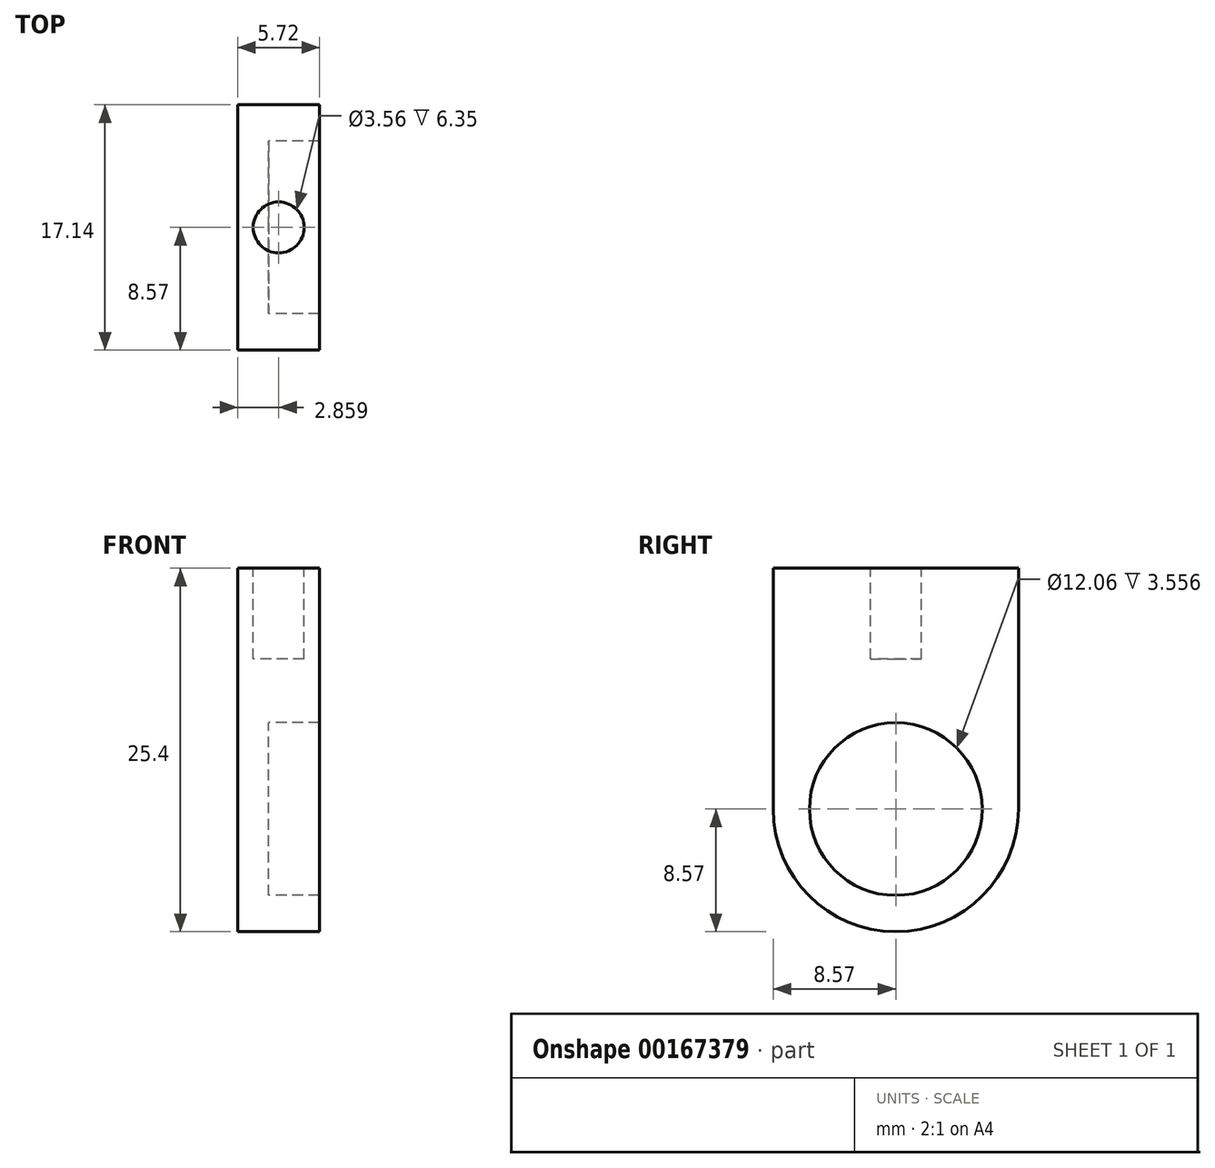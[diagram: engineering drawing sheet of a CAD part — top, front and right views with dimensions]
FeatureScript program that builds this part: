
annotation { "Feature Type Name" : "Feature", "Feature Type Description" : "" }
export const myFeature = defineFeature(function(context is Context, id is Id, definition is map)
    precondition{}
    {
        {
            var Q0;
            Q0=qCreatedBy(makeId("Right.planeOp"),FACE);
            var sketch = newSketch(context, id + "F0", { "sketchPlane" : qUnion([Q0])});
            skCircle(sketch, "E0", {"center": v(0, 0) * mm, "radius": 6.03 * mm});
            skCircle(sketch, "E1", {"center": v(0, 0) * mm, "radius": 8.57 * mm});
            skLineSegment(sketch, "E2.top", {"start": v(-8.57, 16.83) * mm, "end": v(8.57, 16.83) * mm});
            skLineSegment(sketch, "E2.left", {"start": v(-8.57, 0) * mm, "end": v(-8.57, 16.83) * mm});
            skLineSegment(sketch, "E2.right", {"start": v(8.57, 0) * mm, "end": v(8.57, 16.83) * mm});
            skSolve(sketch);
        }
        {
            var Q0;
            Q0 = qSketchRegion(id + "F0", true);
            extrude(context, id + "F1", {"entities" : qUnion([Q0]), "depth" : 3.56 * mm});
        }
        {
            var Q0;
            Q0=makeQuery(id+"F1.opExtrude","CAP_FACE",FACE,{"disambiguationData":[OSD([sQuery(id+"F0.wireOp",EDGE,"E0"),sQuery(id+"F0.wireOp",EDGE,"PU44gY0B-mLXA-vG6P-Z8EY-Ho4tR6I2Q1Xl.bottom"),sQuery(id+"F0.wireOp",EDGE,"PU44gY0B-mLXA-vG6P-Z8EY-Ho4tR6I2Q1Xl.top"),sQuery(id+"F0.wireOp",EDGE,"PU44gY0B-mLXA-vG6P-Z8EY-Ho4tR6I2Q1Xl.left"),sQuery(id+"F0.wireOp",EDGE,"PU44gY0B-mLXA-vG6P-Z8EY-Ho4tR6I2Q1Xl.right")])],"isStart":true});
            var Q1;
            Q1=makeQuery(id+"F0.imprint","IMPRINT",FACE,{"disambiguationData":[TD([[makeQuery(id+"F0.imprint","IMPRINT",EDGE,{"derivedFrom":sQuery(id+"F0.wireOp",EDGE,"E0")}),1.0]])]});
            extrude(context, id + "F2", {"entities" : qUnion([Q0, Q1]), "operationType" : NewBodyOperationType.ADD, "depth" : 2.16 * mm});
        }
        {
            var Q0;
            {var subQ0=sQuery(id+"F0.wireOp",EDGE,"E2.top");Q0=makeQuery(id+"F2.boolean.opBoolean","MERGE",FACE,{"derivedFrom":[makeQuery(id+"F1.opExtrude","SWEPT_FACE",FACE,{"disambiguationData":[OSD([subQ0])]}),makeQuery(id+"F2.opExtrude","SWEPT_FACE",FACE,{"disambiguationData":[OSD([subQ0])]})]});}
            var sketch = newSketch(context, id + "F3", { "sketchPlane" : qUnion([Q0])});
            skCircle(sketch, "E3", {"center": v(0.7, 0) * mm, "radius": 1.78 * mm});
            skPoint(sketch, "E3.centerSnap0", {"position": v(-2.16, 0) * mm});
            skPoint(sketch, "E3.centerSnap1", {"position": v(0.7, 8.57) * mm});
            skSolve(sketch);
        }
        {
            var Q0;
            Q0 = qSketchRegion(id + "F3", true);
            extrude(context, id + "F4", {"entities" : qUnion([Q0]), "operationType" : NewBodyOperationType.REMOVE, "oppositeDirection" : true, "depth" : 6.35 * mm});
        }
    });
